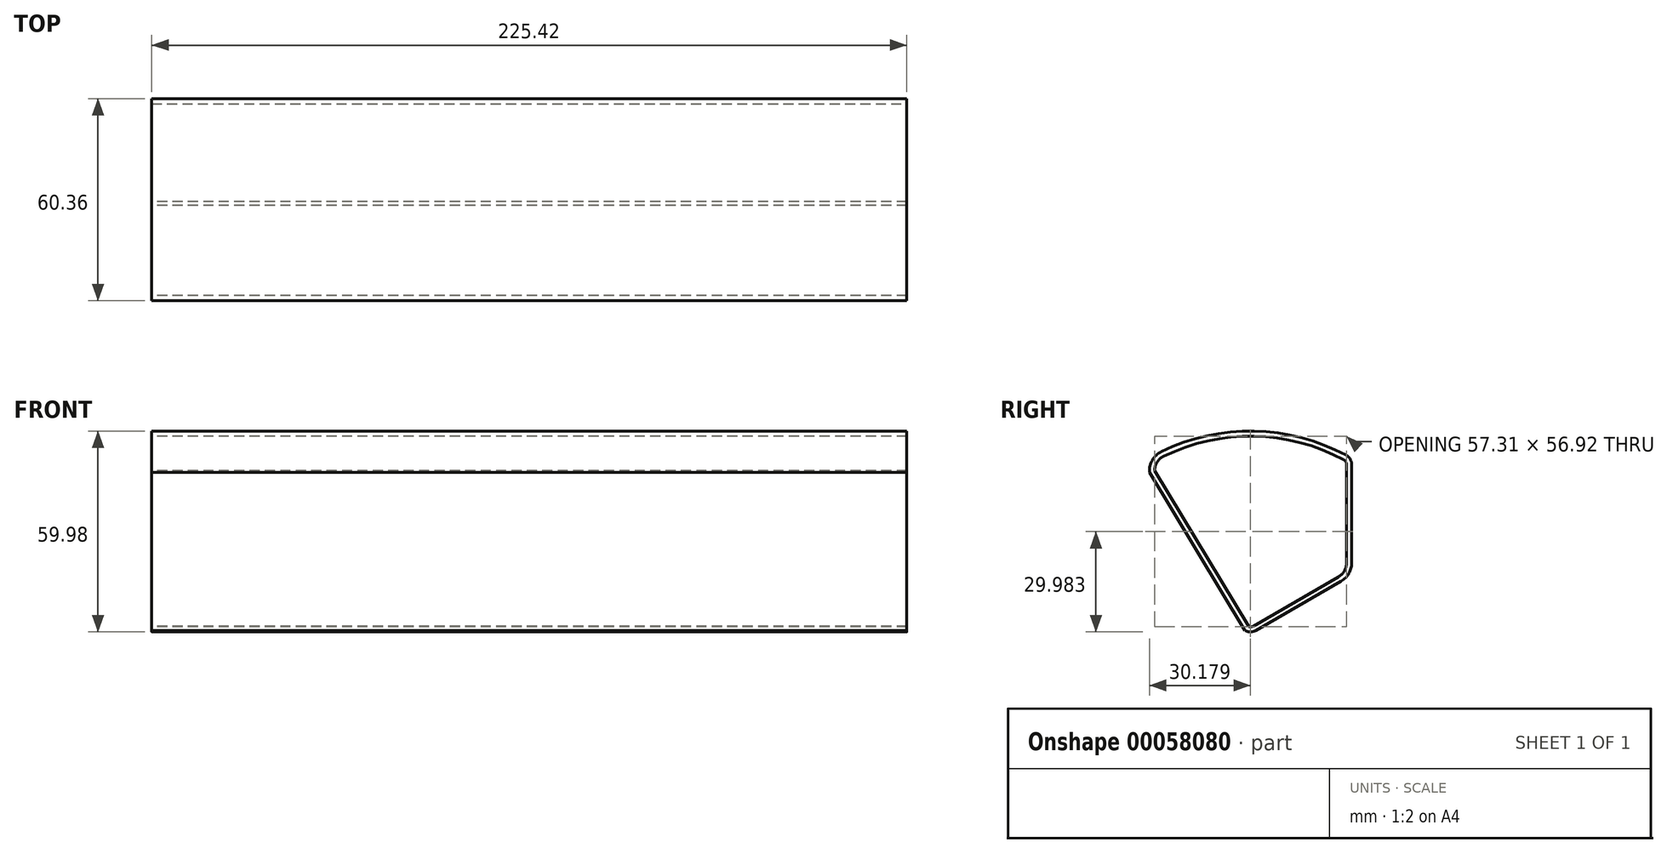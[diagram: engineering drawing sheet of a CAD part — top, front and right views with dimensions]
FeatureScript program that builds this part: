
annotation { "Feature Type Name" : "Feature", "Feature Type Description" : "" }
export const myFeature = defineFeature(function(context is Context, id is Id, definition is map)
    precondition{}
    {
        {
            var Q0;
            Q0=qCreatedBy(makeId("Right.planeOp"),FACE);
            var sketch = newSketch(context, id + "F0", { "sketchPlane" : qUnion([Q0])});
            skLineSegment(sketch, "E0", {"start": v(-30.25, -17.46) * mm, "end": v(0, 0) * mm});
            skLineSegment(sketch, "E1", {"start": v(0, 0) * mm, "end": v(0, 34.93) * mm});
            skArc(sketch, "E2", {"start": v(0, 34.92) * mm, "mid": v(-30.25, 43.03) * mm, "end": v(-60.5, 34.92) * mm});
            skLineSegment(sketch, "E3", {"start": v(0, 34.93) * mm, "end": v(-30.25, -17.46) * mm, "construction": true});
            skPoint(sketch, "E4", {"position": v(-15.12, 8.73) * mm});
            skLineSegment(sketch, "E5", {"start": v(0, 0) * mm, "end": v(-60.5, 34.93) * mm, "construction": true});
            skArc(sketch, "E6", {"start": v(-60.5, 34.92) * mm, "mid": v(-52.39, 4.68) * mm, "end": v(-30.25, -17.46) * mm});
            skLineSegment(sketch, "E7", {"start": v(0, 34.93) * mm, "end": v(-60.5, 34.92) * mm, "construction": true});
            skSolve(sketch);
        }
        {
            var Q0;
            Q0=qSketchRegion(id+"F0",true);
            extrude(context, id + "F1", {"entities" : qUnion([Q0]), "endBound" : BoundingType.SYMMETRIC, "depth" : 225.42 * mm});
        }
        {
            var Q0;
            Q0=makeQuery(id+"F1.opExtrude","SWEPT_EDGE",EDGE,{"disambiguationData":[OSD([sQuery(id+"F0.wireOp",EDGE,"E2"),sQuery(id+"F0.wireOp",EDGE,"E6")])]});
            var Q1;
            Q1=makeQuery(id+"F1.opExtrude","SWEPT_EDGE",EDGE,{"disambiguationData":[OSD([sQuery(id+"F0.wireOp",EDGE,"E0"),sQuery(id+"F0.wireOp",EDGE,"E1")])]});
            fillet(context, id + "F2", {"entities" : qUnion([Q0, Q1]), "radius" : 6.35 * mm, "tangentPropagation" : true, "allowEdgeOverflow" : false});
        }
        {
            var Q0;
            Q0=makeQuery(id+"F1.opExtrude","SWEPT_EDGE",EDGE,{"disambiguationData":[OSD([sQuery(id+"F0.wireOp",EDGE,"E1"),sQuery(id+"F0.wireOp",EDGE,"E2")])]});
            var Q1;
            Q1=makeQuery(id+"F1.opExtrude","SWEPT_EDGE",EDGE,{"disambiguationData":[OSD([sQuery(id+"F0.wireOp",EDGE,"E0"),sQuery(id+"F0.wireOp",EDGE,"E6")])]});
            fillet(context, id + "F3", {"entities" : qUnion([Q0, Q1]), "radius" : 3.17 * mm, "tangentPropagation" : true, "allowEdgeOverflow" : false});
        }
        {
            var Q0;
            Q0=makeQuery(id+"F1.opExtrude","CAP_FACE",FACE,{"disambiguationData":[OSD([sQuery(id+"F0.wireOp",EDGE,"E0"),sQuery(id+"F0.wireOp",EDGE,"E1"),sQuery(id+"F0.wireOp",EDGE,"E2"),sQuery(id+"F0.wireOp",EDGE,"E6")])],"isStart":true});
            var sketch = newSketch(context, id + "F4", { "sketchPlane" : qUnion([Q0])});
            skLineSegment(sketch, "E8", {"start": v(60.35, 30.75) * mm, "end": v(31.9, -16.48) * mm});
            skLineSegment(sketch, "E9", {"start": v(31.9, -16.48) * mm, "end": v(37.58, -19.9) * mm});
            skLineSegment(sketch, "E10", {"start": v(37.58, -19.9) * mm, "end": v(66.04, 27.31) * mm});
            skLineSegment(sketch, "E11", {"start": v(66.04, 27.31) * mm, "end": v(60.35, 30.75) * mm});
            skSolve(sketch);
        }
        {
            var Q0;
            Q0 = qSketchRegion(id + "F4", true);
            var Q1;
            Q1=makeQuery(id+"F1.opExtrude","CAP_FACE",FACE,{"disambiguationData":[OSD([sQuery(id+"F0.wireOp",EDGE,"E0"),sQuery(id+"F0.wireOp",EDGE,"E1"),sQuery(id+"F0.wireOp",EDGE,"E2"),sQuery(id+"F0.wireOp",EDGE,"E6")])],"isStart":false});
            extrude(context, id + "F5", {"entities" : qUnion([Q0]), "operationType" : NewBodyOperationType.REMOVE, "endBound" : BoundingType.UP_TO_SURFACE, "oppositeDirection" : true, "endBoundEntityFace" : qUnion([Q1]), "depth" : 25.4 * mm});
        }
        {
            var Q0;
            Q0=makeQuery(id+"F1.opExtrude","CAP_FACE",FACE,{"disambiguationData":[OSD([sQuery(id+"F0.wireOp",EDGE,"E0"),sQuery(id+"F0.wireOp",EDGE,"E1"),sQuery(id+"F0.wireOp",EDGE,"E2"),sQuery(id+"F0.wireOp",EDGE,"E6")])],"isStart":true});
            var Q1;
            Q1=makeQuery(id+"F1.opExtrude","CAP_FACE",FACE,{"disambiguationData":[OSD([sQuery(id+"F0.wireOp",EDGE,"E0"),sQuery(id+"F0.wireOp",EDGE,"E1"),sQuery(id+"F0.wireOp",EDGE,"E2"),sQuery(id+"F0.wireOp",EDGE,"E6")])],"isStart":false});
            shell(context, id + "F6", {"entities" : qUnion([Q0, Q1]), "thickness" : 1.52 * mm});
        }
    });
